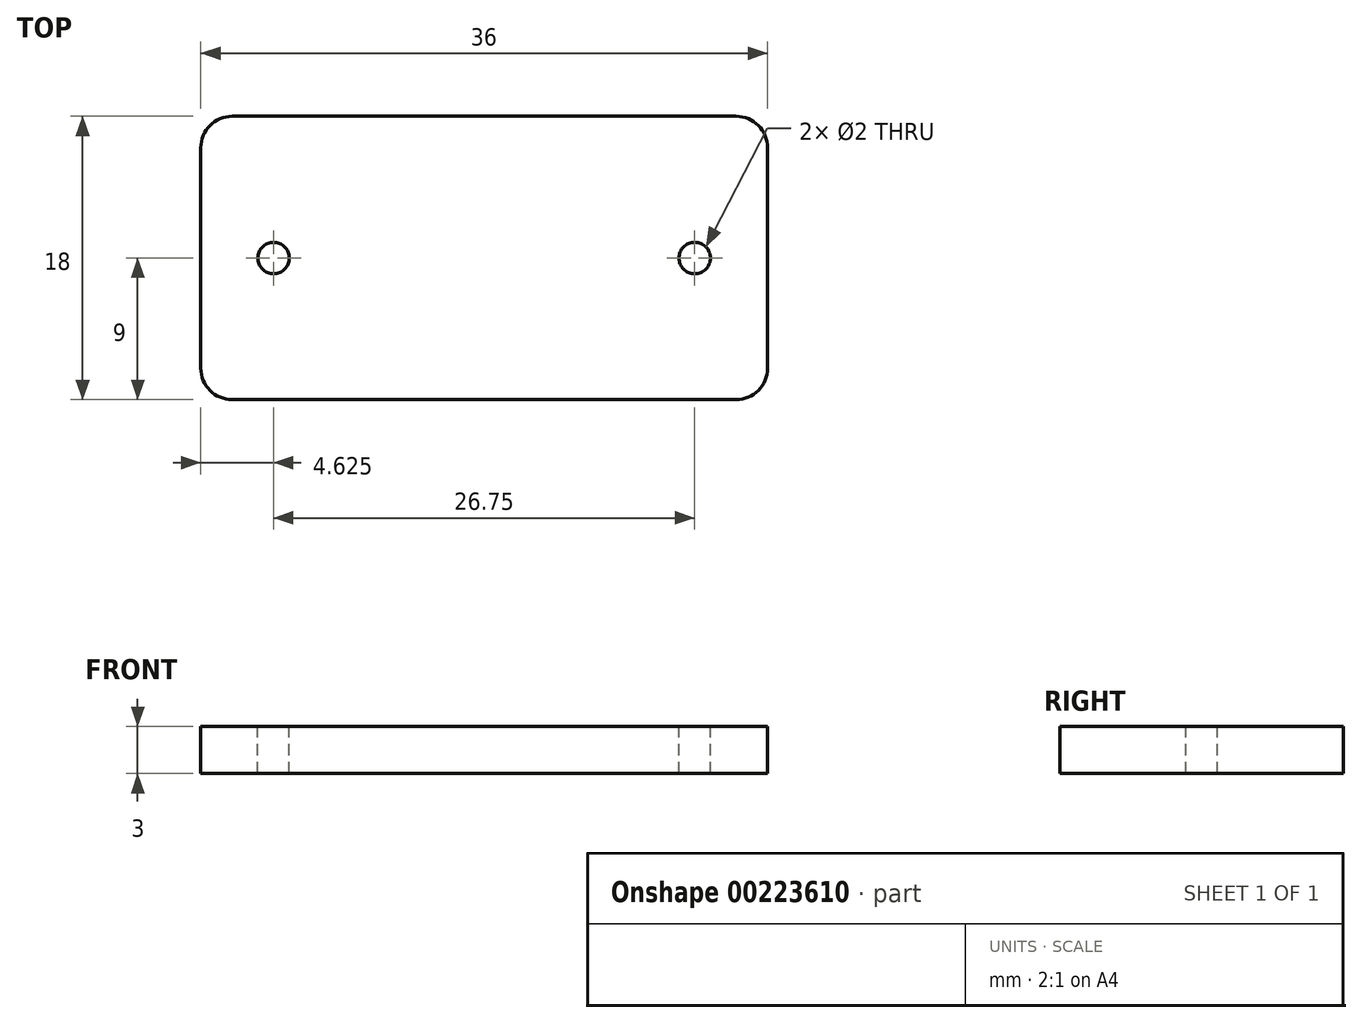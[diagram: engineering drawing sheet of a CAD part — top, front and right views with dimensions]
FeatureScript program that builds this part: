
annotation { "Feature Type Name" : "Feature", "Feature Type Description" : "" }
export const myFeature = defineFeature(function(context is Context, id is Id, definition is map)
    precondition{}
    {
        {
            var Q0;
            Q0=qCreatedBy(makeId("Top.planeOp"),FACE);
            var sketch = newSketch(context, id + "F0", { "sketchPlane" : qUnion([Q0])});
            skLineSegment(sketch, "E0.bottom", {"start": v(16, -9) * mm, "end": v(-16, -9) * mm});
            skLineSegment(sketch, "E0.top", {"start": v(16, 9) * mm, "end": v(-16, 9) * mm});
            skLineSegment(sketch, "E0.left", {"start": v(18, -7) * mm, "end": v(18, 7) * mm});
            skLineSegment(sketch, "E0.right", {"start": v(-18, -7) * mm, "end": v(-18, 7) * mm});
            skPoint(sketch, "E0.middle", {"position": v(0, 0) * mm});
            skPoint(sketch, "E1.visualSharp", {"position": v(-18, 9) * mm});
            skArc(sketch, "E1.filletArc", {"start": v(-16, 9) * mm, "mid": v(-17.41, 8.41) * mm, "end": v(-18, 7) * mm});
            skPoint(sketch, "E2.visualSharp", {"position": v(18, 9) * mm});
            skArc(sketch, "E2.filletArc", {"start": v(18, 7) * mm, "mid": v(17.41, 8.41) * mm, "end": v(16, 9) * mm});
            skPoint(sketch, "E3.visualSharp", {"position": v(18, -9) * mm});
            skArc(sketch, "E3.filletArc", {"start": v(16, -9) * mm, "mid": v(17.41, -8.41) * mm, "end": v(18, -7) * mm});
            skPoint(sketch, "E4.visualSharp", {"position": v(-18, -9) * mm});
            skArc(sketch, "E4.filletArc", {"start": v(-18, -7) * mm, "mid": v(-17.41, -8.41) * mm, "end": v(-16, -9) * mm});
            skSolve(sketch);
        }
        {
            var Q0;
            Q0 = qSketchRegion(id + "F0", true);
            extrude(context, id + "F1", {"entities" : qUnion([Q0]), "depth" : 3 * mm});
        }
        {
            var Q0;
            Q0=makeQuery(id+"F1.opExtrude","CAP_FACE",FACE,{"disambiguationData":[OSD([sQuery(id+"F0.wireOp",EDGE,"E0.bottom"),sQuery(id+"F0.wireOp",EDGE,"E0.top"),sQuery(id+"F0.wireOp",EDGE,"E0.left"),sQuery(id+"F0.wireOp",EDGE,"E0.right"),sQuery(id+"F0.wireOp",EDGE,"E1.filletArc"),sQuery(id+"F0.wireOp",EDGE,"E2.filletArc"),sQuery(id+"F0.wireOp",EDGE,"E3.filletArc"),sQuery(id+"F0.wireOp",EDGE,"E4.filletArc")])],"isStart":false});
            var sketch = newSketch(context, id + "F2", { "sketchPlane" : qUnion([Q0])});
            skCircle(sketch, "E5", {"center": v(13.37, 0) * mm, "radius": 1 * mm});
            skCircle(sketch, "E6", {"center": v(-13.37, 0) * mm, "radius": 1 * mm});
            skLineSegment(sketch, "E7", {"start": v(-13.37, 0) * mm, "end": v(0, 0) * mm, "construction": true});
            skLineSegment(sketch, "E8", {"start": v(0, 0) * mm, "end": v(13.37, 0) * mm, "construction": true});
            skSolve(sketch);
        }
        {
            var Q0;
            Q0 = qSketchRegion(id + "F2", true);
            extrude(context, id + "F3", {"entities" : qUnion([Q0]), "operationType" : NewBodyOperationType.REMOVE, "endBound" : BoundingType.UP_TO_NEXT, "oppositeDirection" : true, "depth" : 25 * mm});
        }
    });
